# Revit family: sh-230M-230v
name_source: partatom
category: Lighting Fixtures
revit_build: Autodesk Revit 2017 (Build: 20160225_1515(x64)
units: mm (PartAtom-declared; Revit-internal decimal feet)

## family parameters
Always vertical = Yes
Cut with Voids When Loaded = No
Host = Ceiling
Light Source = Yes
OmniClass Number = 23.80.70.11
OmniClass Title = Luminaries for Internal Lighting
Part Type = Normal
Room Calculation Point = No
Round Connector Dimension = Use Diameter
Shared = No

## types (2) — shared parameters
Body Material = ABS
Color Filter = 16777215
Default Elevation = 0.0 cm
Dimming Lamp Color Temperature Shift = <None>
Emit Shape Visible in Rendering = No
Flicker = Free Flicker
IP = IP65
Lamp = LED
Manufacturer = SHOA
Model = Sh-230M-230V
Photometric Web File = SH 230M.ies
Protection Class = Class II
Tilt Angle = 90.00°
Type medule = SMD
Voltage/Frequency = 230V-50HZ
color rendering index(CRI) = 80
color temperature = 4000K
consumption current = 0 A
instalation = Surface Mounted
wattage. = 12 W
website = www.shoaco.com

## per-type parameters (varying)
| type | Body color | Emit from Circle Diameter |
| SH-230M-ND(Black body-4000K-LED) | black body | 61.0 cm |
| SH-230M-ND(white body-4000K-LED) | white body | 10.0 cm |

## geometry (parser evidence)
native form markers: Sweep x2
no freeform markers — native parametric forms only
